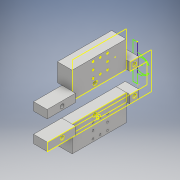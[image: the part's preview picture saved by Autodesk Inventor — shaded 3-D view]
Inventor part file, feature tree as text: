
AUTODESK INVENTOR PART (.ipt)
format: ipt  version: 2017 (Build 210142000, 142)  size: 404,480 bytes
history: native  units: mm
features: sketch x19, extrude x13, projected_geometry x8
ambient origin geometry x8: Origin, YZ Plane, XZ Plane, XY Plane, X Axis, Y Axis, Z Axis, Center Point
bodies: Solide1 (feature_tree)
feature tree (40):
  extrude  "Extrusion1"  Depth=5.0mm
  sketch  "Esquisse2"
  sketch  "Esquisse3"
  extrude  "Extrusion2"  Depth=5.0mm
  extrude  "Extrusion3"  Depth=110.0mm
  extrude  "Extrusion4"  Depth=9.0mm
  extrude  "Extrusion5"  Depth=110.0mm
  sketch  "Esquisse8"
  sketch  "Esquisse9"
  extrude  "Extrusion6"  Depth=40.148494mm
  sketch  "Esquisse11"
  extrude  "Extrusion7"  Depth=9.0mm
  extrude  "Extrusion8"  Depth=15.0mm TaperAngle=0.0deg
  extrude  "Extrusion9"  Depth=12.0mm
  extrude  "Extrusion10"  Depth=15.0mm TaperAngle=0.0deg
  extrude  "Extrusion11"  Depth=3.8mm
  extrude  "Extrusion12"  Depth=60.0mm
  extrude  "Extrusion13"  Depth=15.0mm TaperAngle=0.0deg
  sketch  "Esquisse1"
  sketch  "Esquisse4"
  sketch  "Esquisse5"
  sketch  "Esquisse6"
  sketch  "Esquisse7"
  projected_geometry  "Boucle projetée1"
  projected_geometry  "Boucle projetée2"
  projected_geometry  "Boucle projetée3"
  sketch  "Esquisse10"
  projected_geometry  "Boucle projetée4"
  sketch  "Esquisse13"
  sketch  "Esquisse14"
  sketch  "Esquisse15"
  sketch  "Esquisse16"
  projected_geometry  "Boucle projetée5"
  sketch  "Esquisse17"
  projected_geometry  "Boucle projetée6"
  projected_geometry  "Boucle projetée7"
  sketch  "Esquisse18"
  projected_geometry  "Boucle projetée8"
  sketch  "Esquisse19"
  sketch  "Esquisse12"
